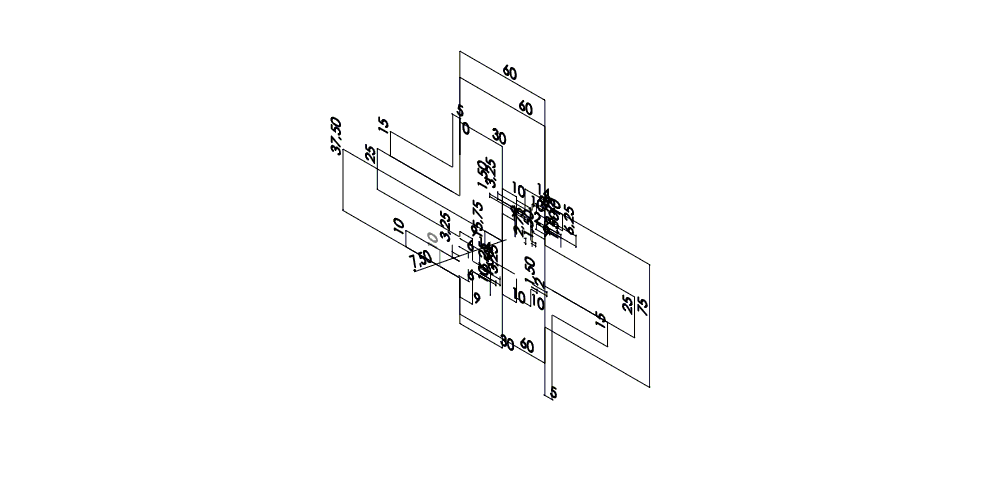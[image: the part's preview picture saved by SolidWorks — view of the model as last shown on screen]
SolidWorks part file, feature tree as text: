
SOLIDWORKS PART (.sldprt)
format: sldprt  version: not decoded by parser v0  size: 346,624 bytes
history: native  units: mm
features: extrude x56, fillet x2, material x1, sketch x1 (+13 scaffold rows collapsed)
feature tree (73):
  scaffold x13  (default folders/planes/origin — collapsed)
  material  "Matériau <non spécifié>"
  sketch  "Esquisse1"  dims[c1.D1=~4.13282mm c1.D28=7.5mm c1.D21=~5.091304mm c2.D1=30.0mm c2.D2=60.0mm c2.D3=60.0mm c2.D4=30.0mm c2.D5=60.0mm c2.D6=0.0mm c2.D7=5.0mm c2.D8=5.0mm c2.D9=5.0mm c2.D10=0.0mm c2.D11=75.0mm c2.D12=15.0mm c2.D13=15.0mm c2.D14=15.0mm c2.D15=15.0mm c2.D16=25.0mm c2.D17=25.0mm c2.D18=10.0mm c2.D19=37.5mm c2.D20=9.0mm c2.D21=6.75mm c2.D22=15.75mm c2.D23=12.0mm c2.D24=1.5mm c2.D25=1.5mm c2.D26=2.0mm c2.D27=2.0mm c2.D29=10.0mm c2.D30=10.0mm c2.D31=10.0mm c2.D32=10.0mm c3.D6=3.25mm c3.D12=14.0mm c3.D33=6.25mm c3.D34=1.5mm c3.D35=10.0mm c3.D36=~2.445726mm c4.D36=90.0deg c5.D36=1.5mm c5.D37=3.25mm c5.D9=9.0mm c5.D14=6.0mm c5.D38=6.0mm c5.D39=9.0mm c5.D40=14.0mm c5.D41=3.25mm c5.D42=10.0mm c5.D43=6.0mm c5.D44=6.0mm c5.D45=9.0mm c5.D46=9.0mm c5.D47=6.25mm c5.D48=1.5mm c5.D49=3.25mm c5.D50=10.0mm c5.D51=9.0mm c5.D21=3.0mm]
  extrude  "Boss.-Extru.1"  Depth=3mm flange_len_value=0
  extrude  "Associativity_IDs"  Depth=0 flange_len_value=0 7b5b9a7a-6b5a-4703-a7f1-16a8fcbd6f68=0deg
  extrude  "Associativity_IDs"  Depth=0 flange_len_value=0 176a5910-1771-4c9f-bdb7-0e19523b7314=0deg
  extrude  "Associativity_IDs"  Depth=0 flange_len_value=0 55f2f1b8-48ba-4533-9585-3583c4a4a523=0deg
  extrude  "Associativity_IDs"  Depth=0 flange_len_value=0 6b9459d0-39da-449c-b8d6-8250549f467c=0deg
  extrude  "Associativity_IDs"  Depth=0 flange_len_value=0 fed3911d-3253-4aab-8e42-eb9aa4f0500e=0deg
  extrude  "Associativity_IDs"  Depth=0 flange_len_value=0 01c1dcc7-ad16-482e-922e-9b7322365338=0deg
  extrude  "Associativity_IDs"  Depth=0 flange_len_value=0 c0a57a2e-e67a-474e-be09-1750633cbec8=0deg
  extrude  "Associativity_IDs"  Depth=0 flange_len_value=0 5ee7a49e-76cc-4686-a07e-c5c970472c83=0deg
  extrude  "Associativity_IDs"  Depth=0 flange_len_value=0 424bbb98-513e-4afb-809f-5b97ef7dc834=0deg
  extrude  "Associativity_IDs"  Depth=0 flange_len_value=0 6af14341-d8f8-42b1-90c5-f51fed845649=0deg
  extrude  "Associativity_IDs"  Depth=0 flange_len_value=0 8a6961dd-2b75-46e2-8b27-dae5db3de140=0deg
  extrude  "Associativity_IDs"  Depth=0 flange_len_value=0 b28be8aa-971a-4bee-976d-b8c9f1a67758=0deg
  extrude  "Associativity_IDs"  Depth=0 flange_len_value=0 2dca65f9-27e3-49fb-a927-ab3328c16b11=0deg
  extrude  "Associativity_IDs"  Depth=0 flange_len_value=0 204c4c6c-fd91-4d4f-8a97-49ae31bec871=0deg
  extrude  "Associativity_IDs"  Depth=0 flange_len_value=0 2a793f01-6a3d-411a-91e1-808c2c61d737=0deg
  extrude  "Associativity_IDs"  Depth=0 flange_len_value=0 70981b76-4107-4e1c-90ae-482650940e71=0deg
  extrude  "Associativity_IDs"  Depth=0 flange_len_value=0 c7cd9464-bcc7-44d2-8a59-1f72992e1938=0deg
  extrude  "Associativity_IDs"  Depth=0 flange_len_value=0 3f2323d7-4697-49b9-afc7-286c4a2e2445=0deg
  extrude  "Associativity_IDs"  Depth=0 flange_len_value=0 1b8ce68f-559c-4b60-aa33-7342e44fd3df=0deg
  extrude  "Associativity_IDs"  Depth=0 flange_len_value=0 3d762841-fca2-4f8c-9de0-4f15220ab875=0deg
  extrude  "Associativity_IDs"  Depth=0 flange_len_value=0 5ffb295a-90f8-4586-a5b3-b48994a75ebe=0deg
  extrude  "Associativity_IDs"  Depth=0 flange_len_value=0 4c897013-619a-465b-bdb0-0c5ad73f6ad2=0deg
  extrude  "Associativity_IDs"  Depth=0 flange_len_value=0 65e86ee3-15f1-4278-8d54-6dab3d384a50=0deg
  extrude  "Associativity_IDs"  Depth=0 flange_len_value=0 e4d73b62-8ddd-40b5-a7c5-45ccc09780f9=0deg
  extrude  "Associativity_IDs"  Depth=0 flange_len_value=0 d9c75ca3-5b77-41a7-b336-2fea266672ea=0deg
  extrude  "Associativity_IDs"  Depth=0 flange_len_value=0 da13cb5e-b4ae-469e-99fe-e822a64a8c32=0deg
  extrude  "Associativity_IDs"  Depth=0 flange_len_value=0 0aa9e9df-0192-493c-a74c-72bfc40c6bdf=0deg
  extrude  "Associativity_IDs"  Depth=0 flange_len_value=0 22c9b65e-c120-4a23-94a8-c2b33b7a8d1f=0deg
  extrude  "Associativity_IDs"  Depth=0 flange_len_value=0 38e9e832-f6c9-4baa-89aa-d808d56dc3e3=0deg
  extrude  "Associativity_IDs"  Depth=0 flange_len_value=0 4fcbd7b1-123a-47de-9e97-8567ec107c34=0deg
  extrude  "Associativity_IDs"  Depth=0 flange_len_value=0 5eb759f6-996f-4e99-a1dd-77f5c8365c23=0deg
  extrude  "Associativity_IDs"  Depth=0 flange_len_value=0 b0e11f2b-9f79-4e2d-87f7-63db912a61e0=0deg
  extrude  "Associativity_IDs"  Depth=0 flange_len_value=0 6b3ca976-8031-4464-94c3-d1e12c11ee86=0deg
  extrude  "Associativity_IDs"  Depth=0 flange_len_value=0 4e993720-89ae-4998-8d76-750d54e56dcb=0deg
  extrude  "Associativity_IDs"  Depth=0 flange_len_value=0 7fe8b40e-4bf1-4667-a522-04a6adb00757=0deg
  extrude  "Associativity_IDs"  Depth=0 flange_len_value=0 8d4b0540-1911-4ecc-8082-78400e28c590=0deg
  extrude  "Associativity_IDs"  Depth=0 flange_len_value=0 d6a30cbb-8318-42c5-9714-65bcc424146e=0deg
  extrude  "Associativity_IDs"  Depth=0 flange_len_value=0 81577c91-152f-478b-b7d0-f029ac91c841=0deg
  extrude  "Associativity_IDs"  Depth=0 flange_len_value=0 a0b2d769-3a5d-4f06-9b37-85e8f09ae4b4=0deg
  extrude  "Associativity_IDs"  Depth=0 flange_len_value=0 5f413a28-40a2-45ad-a3ec-3f047b5ba547=0deg
  extrude  "Associativity_IDs"  Depth=0 flange_len_value=0 2ac5d8b6-85fc-4829-b017-9141e2f98708=0deg
  extrude  "Associativity_IDs"  Depth=0 flange_len_value=0 9e3fb473-5a04-46e8-a456-a490d0ac1727=0deg
  extrude  "Associativity_IDs"  Depth=0 flange_len_value=0 75b4db01-bc70-4fe2-91fb-96717001b548=0deg
  extrude  "Associativity_IDs"  Depth=0 flange_len_value=0 c8617c1f-8a71-4117-8c00-82342d8b5fcc=0deg
  extrude  "Associativity_IDs"  Depth=0 flange_len_value=0 13622363-12a9-4fdd-92fb-69167adbf8cb=0deg
  extrude  "Associativity_IDs"  Depth=0 flange_len_value=0 325566df-48b1-41a7-8958-64f025d704cd=0deg
  extrude  "Associativity_IDs"  Depth=0 flange_len_value=0 a950ccc2-66d2-42b4-a198-d3d337793003=0deg
  extrude  "Associativity_IDs"  Depth=0 flange_len_value=0 6171f407-7809-4fab-8fc7-64ace0d4dbc0=0deg
  extrude  "Associativity_IDs"  Depth=0 flange_len_value=0 3e2d44bb-0998-4234-a36e-5b05816350a1=0deg
  extrude  "Associativity_IDs"  Depth=0 flange_len_value=0 78089c76-0987-42d5-a211-5c73491ba3e0=0deg
  extrude  "Associativity_IDs"  Depth=0 flange_len_value=0 b4449fc3-c962-484d-8073-631604675616=0deg
  extrude  "Associativity_IDs"  Depth=0 flange_len_value=0 3a9de56f-edab-4618-853d-8edfcb2c7e81=0deg
  extrude  "Associativity_IDs"  Depth=0 flange_len_value=0 a778f70b-7c71-4833-b151-8150f8be4ca0=0deg
  extrude  "Associativity_IDs"  Depth=0 flange_len_value=0 a8ad569c-5792-4e13-84ff-fe69e7781099=0deg
  extrude  "Associativity_IDs"  Depth=0 flange_len_value=0
  fillet  "Congé3"  Radius=1mm
  fillet  "Congé4"  Radius=1mm
decode coverage: 59 of 59 modeling features carry decoded parameters
note: ~ marks probable driven/reference dimensions
note: suppression state not decoded; provenance and decode notes live in map.json
